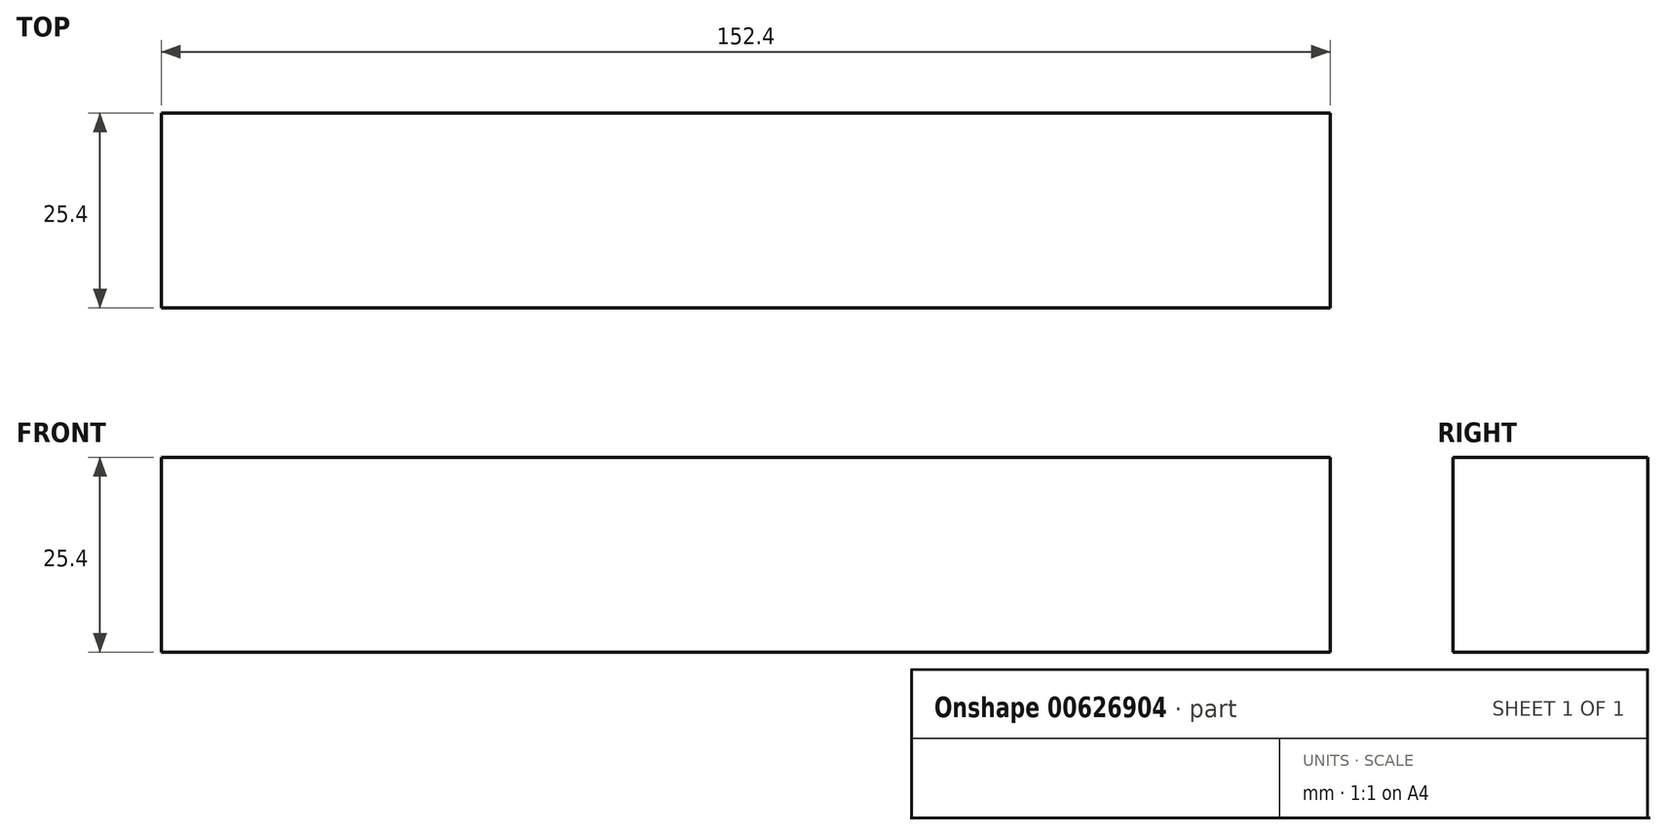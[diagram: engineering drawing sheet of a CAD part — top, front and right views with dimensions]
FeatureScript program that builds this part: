
annotation { "Feature Type Name" : "Feature", "Feature Type Description" : "" }
export const myFeature = defineFeature(function(context is Context, id is Id, definition is map)
    precondition{}
    {
        {
            var Q0;
            Q0=qCreatedBy(makeId("Right.planeOp"),FACE);
            var sketch = newSketch(context, id + "F0", { "sketchPlane" : qUnion([Q0])});
            skLineSegment(sketch, "E0.bottom", {"start": v(0, 0) * mm, "end": v(25.4, 0) * mm});
            skLineSegment(sketch, "E0.top", {"start": v(0, 25.4) * mm, "end": v(25.4, 25.4) * mm});
            skLineSegment(sketch, "E0.left", {"start": v(0, 0) * mm, "end": v(0, 25.4) * mm});
            skLineSegment(sketch, "E0.right", {"start": v(25.4, 0) * mm, "end": v(25.4, 25.4) * mm});
            skSolve(sketch);
        }
        {
            var Q0;
            Q0 = qSketchRegion(id + "F0", true);
            extrude(context, id + "F1", {"entities" : qUnion([Q0]), "depth" : 152.4 * mm, "offsetDistance" : 25.4 * mm});
        }
    });
